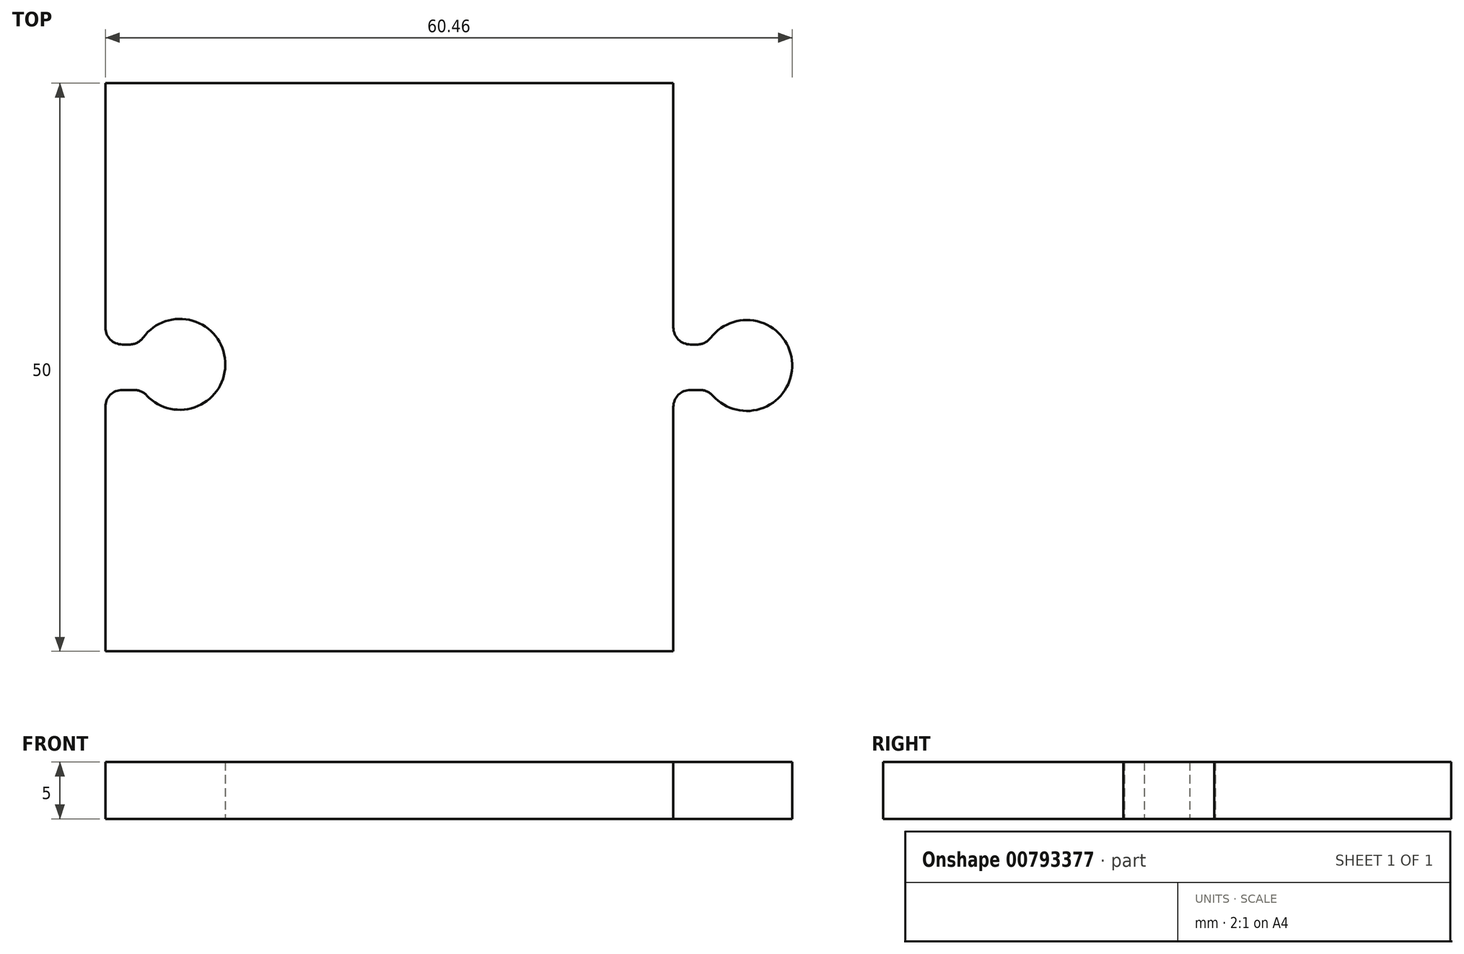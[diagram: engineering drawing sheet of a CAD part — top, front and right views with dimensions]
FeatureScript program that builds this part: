
annotation { "Feature Type Name" : "Feature", "Feature Type Description" : "" }
export const myFeature = defineFeature(function(context is Context, id is Id, definition is map)
    precondition{}
    {
        {
            var Q0;
            Q0=qCreatedBy(makeId("Top.planeOp"),FACE);
            var sketch = newSketch(context, id + "F0", { "sketchPlane" : qUnion([Q0])});
            skLineSegment(sketch, "E0", {"start": v(0, 50) * mm, "end": v(-50, 50) * mm});
            skLineSegment(sketch, "E1", {"start": v(-50, 50) * mm, "end": v(-50, 28.5) * mm});
            skLineSegment(sketch, "E2", {"start": v(0, 0) * mm, "end": v(-50, 0) * mm});
            skLineSegment(sketch, "E3", {"start": v(-50, 0) * mm, "end": v(-50, 21.5) * mm});
            skLineSegment(sketch, "E4", {"start": v(-48.5, 23) * mm, "end": v(-47.46, 23) * mm});
            skLineSegment(sketch, "E5", {"start": v(-48.5, 27) * mm, "end": v(-47.88, 27) * mm});
            skPoint(sketch, "E6.visualSharp", {"position": v(-50, 27) * mm});
            skArc(sketch, "E6.filletArc", {"start": v(-50, 28.5) * mm, "mid": v(-49.56, 27.44) * mm, "end": v(-48.5, 27) * mm});
            skPoint(sketch, "E7.visualSharp", {"position": v(-50, 23) * mm});
            skArc(sketch, "E7.filletArc", {"start": v(-48.5, 23) * mm, "mid": v(-49.56, 22.56) * mm, "end": v(-50, 21.5) * mm});
            skArc(sketch, "E8", {"start": v(-46.36, 22.52) * mm, "mid": v(-39.45, 25.5) * mm, "end": v(-46.67, 27.61) * mm});
            skLineSegment(sketch, "E9.trimOffspring", {"start": v(-41.71, 23) * mm, "end": v(-39.54, 23) * mm});
            skLineSegment(sketch, "E10.trimOffspring", {"start": v(-39.84, 27) * mm, "end": v(-39.54, 27) * mm});
            skPoint(sketch, "E11.visualSharp", {"position": v(-46.74, 23) * mm});
            skArc(sketch, "E11.filletArc", {"start": v(-46.36, 22.52) * mm, "mid": v(-46.86, 22.88) * mm, "end": v(-47.46, 23) * mm});
            skPoint(sketch, "E12.visualSharp", {"position": v(-47.04, 27) * mm});
            skArc(sketch, "E12.filletArc", {"start": v(-47.88, 27) * mm, "mid": v(-47.2, 27.16) * mm, "end": v(-46.67, 27.61) * mm});
            skPoint(sketch, "E13.end.orphan", {"position": v(9.9, 27) * mm});
            skPoint(sketch, "E14.end.orphan", {"position": v(9.9, 23) * mm});
            skLineSegment(sketch, "E15", {"start": v(0, 50) * mm, "end": v(0, 28.5) * mm});
            skLineSegment(sketch, "E16", {"start": v(0, 0) * mm, "end": v(0, 21.5) * mm});
            skLineSegment(sketch, "E17", {"start": v(1.5, 23) * mm, "end": v(2.35, 23) * mm});
            skLineSegment(sketch, "E18", {"start": v(1.5, 27) * mm, "end": v(2.1, 27) * mm});
            skArc(sketch, "E19", {"start": v(3.47, 22.5) * mm, "mid": v(10.46, 25.3) * mm, "end": v(3.29, 27.59) * mm});
            skLineSegment(sketch, "E20.trimOffspring", {"start": v(9.83, 23) * mm, "end": v(9.9, 23) * mm});
            skPoint(sketch, "E21.visualSharp", {"position": v(0, 27) * mm});
            skArc(sketch, "E21.filletArc", {"start": v(0, 28.5) * mm, "mid": v(0.44, 27.44) * mm, "end": v(1.5, 27) * mm});
            skPoint(sketch, "E22.visualSharp", {"position": v(0, 23) * mm});
            skArc(sketch, "E22.filletArc", {"start": v(1.5, 23) * mm, "mid": v(0.44, 22.56) * mm, "end": v(0, 21.5) * mm});
            skPoint(sketch, "E23.visualSharp", {"position": v(2.91, 27) * mm});
            skArc(sketch, "E23.filletArc", {"start": v(2.1, 27) * mm, "mid": v(2.76, 27.15) * mm, "end": v(3.29, 27.59) * mm});
            skPoint(sketch, "E24.visualSharp", {"position": v(3.09, 23) * mm});
            skArc(sketch, "E24.filletArc", {"start": v(3.47, 22.5) * mm, "mid": v(2.96, 22.87) * mm, "end": v(2.35, 23) * mm});
            skSolve(sketch);
        }
        {
            var Q0;
            Q0 = qSketchRegion(id + "F0", true);
            extrude(context, id + "F1", {"entities" : qUnion([Q0]), "depth" : 5 * mm, "offsetDistance" : 25 * mm});
        }
    });
